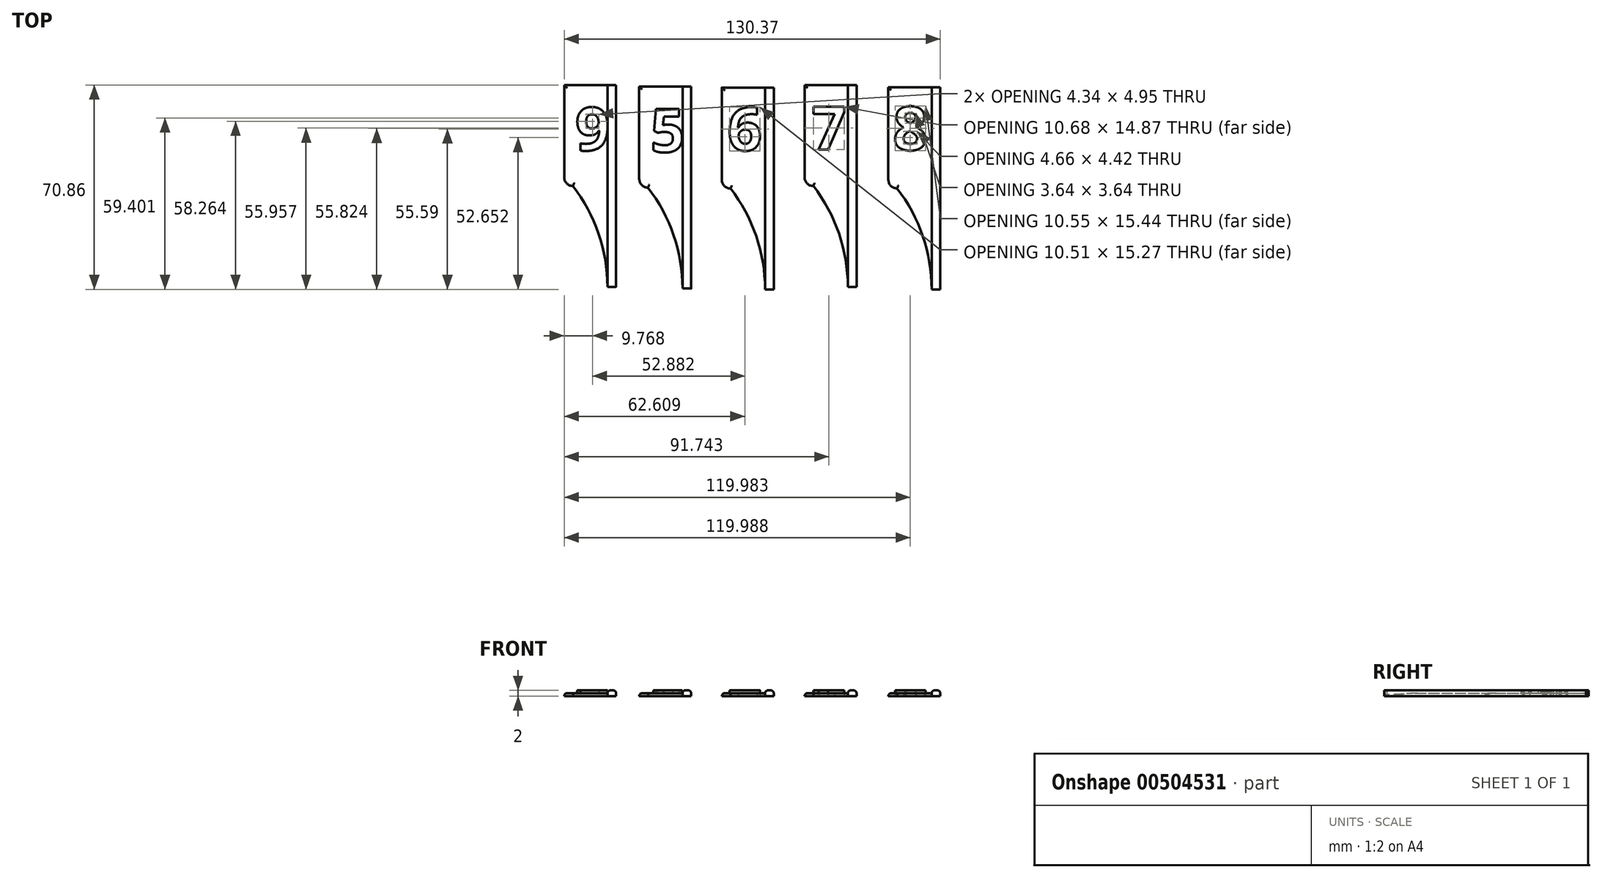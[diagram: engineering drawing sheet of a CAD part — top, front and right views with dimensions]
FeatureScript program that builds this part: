
annotation { "Feature Type Name" : "Feature", "Feature Type Description" : "" }
export const myFeature = defineFeature(function(context is Context, id is Id, definition is map)
    precondition{}
    {
        {
            var Q0;
            Q0=qCreatedBy(makeId("Top.planeOp"),FACE);
            var sketch = newSketch(context, id + "F0", { "sketchPlane" : qUnion([Q0])});
            skLineSegment(sketch, "E0.bottom", {"start": v(-42.45, -18.74) * mm, "end": v(-30.45, -18.74) * mm});
            skLineSegment(sketch, "E0.top", {"start": v(-45.45, 16.26) * mm, "end": v(-30.45, 16.26) * mm});
            skLineSegment(sketch, "E0.left", {"start": v(-45.45, -15.74) * mm, "end": v(-45.45, 16.26) * mm});
            skLineSegment(sketch, "E0.right", {"start": v(-30.45, -18.74) * mm, "end": v(-30.45, 16.26) * mm});
            skLineSegment(sketch, "E1.bottom", {"start": v(-30.45, 16.26) * mm, "end": v(-27.45, 16.26) * mm});
            skLineSegment(sketch, "E1.top", {"start": v(-30.45, -53.74) * mm, "end": v(-27.45, -53.74) * mm});
            skLineSegment(sketch, "E1.left", {"start": v(-30.45, 16.26) * mm, "end": v(-30.45, -53.74) * mm});
            skLineSegment(sketch, "E1.right", {"start": v(-27.45, 16.26) * mm, "end": v(-27.45, -53.74) * mm});
            skPoint(sketch, "E2.visualSharp", {"position": v(-45.45, -18.74) * mm});
            skArc(sketch, "E2.filletArc", {"start": v(-45.45, -15.74) * mm, "mid": v(-44.57, -17.86) * mm, "end": v(-42.45, -18.74) * mm});
            skArc(sketch, "E3", {"start": v(-30.45, -53.74) * mm, "mid": v(-33.53, -35.24) * mm, "end": v(-42.45, -18.74) * mm});
            skText(sketch, "E4", { "text": "5", "fontName": "OpenSans-Bold.ttf"});
            skLineSegment(sketch, "E5.bottom", {"start": v(-13.82, -19.04) * mm, "end": v(-1.82, -19.04) * mm});
            skLineSegment(sketch, "E5.top", {"start": v(-16.82, 15.96) * mm, "end": v(-1.82, 15.96) * mm});
            skLineSegment(sketch, "E5.left", {"start": v(-16.82, -16.04) * mm, "end": v(-16.82, 15.96) * mm});
            skLineSegment(sketch, "E5.right", {"start": v(-1.82, -19.04) * mm, "end": v(-1.82, 15.96) * mm});
            skLineSegment(sketch, "E6.bottom", {"start": v(-1.82, 15.96) * mm, "end": v(1.18, 15.96) * mm});
            skLineSegment(sketch, "E6.top", {"start": v(-1.82, -54.04) * mm, "end": v(1.18, -54.04) * mm});
            skLineSegment(sketch, "E6.left", {"start": v(-1.82, 15.96) * mm, "end": v(-1.82, -54.04) * mm});
            skLineSegment(sketch, "E6.right", {"start": v(1.18, 15.96) * mm, "end": v(1.18, -54.04) * mm});
            skPoint(sketch, "E7.visualSharp", {"position": v(-16.82, -19.04) * mm});
            skArc(sketch, "E7.filletArc", {"start": v(-16.82, -16.04) * mm, "mid": v(-15.94, -18.16) * mm, "end": v(-13.82, -19.04) * mm});
            skArc(sketch, "E8", {"start": v(-1.82, -54.04) * mm, "mid": v(-4.9, -35.54) * mm, "end": v(-13.82, -19.04) * mm});
            skText(sketch, "E9", { "text": "6", "fontName": "OpenSans-Bold.ttf"});
            skLineSegment(sketch, "E10.bottom", {"start": v(14.88, -18.18) * mm, "end": v(26.88, -18.18) * mm});
            skLineSegment(sketch, "E10.top", {"start": v(11.88, 16.82) * mm, "end": v(26.88, 16.82) * mm});
            skLineSegment(sketch, "E10.left", {"start": v(11.88, -15.18) * mm, "end": v(11.88, 16.82) * mm});
            skLineSegment(sketch, "E10.right", {"start": v(26.88, -18.18) * mm, "end": v(26.88, 16.82) * mm});
            skLineSegment(sketch, "E11.bottom", {"start": v(26.88, 16.82) * mm, "end": v(29.88, 16.82) * mm});
            skLineSegment(sketch, "E11.top", {"start": v(26.88, -53.18) * mm, "end": v(29.88, -53.18) * mm});
            skLineSegment(sketch, "E11.left", {"start": v(26.88, 16.82) * mm, "end": v(26.88, -53.18) * mm});
            skLineSegment(sketch, "E11.right", {"start": v(29.88, 16.82) * mm, "end": v(29.88, -53.18) * mm});
            skPoint(sketch, "E12.visualSharp", {"position": v(11.88, -18.18) * mm});
            skArc(sketch, "E12.filletArc", {"start": v(11.88, -15.18) * mm, "mid": v(12.76, -17.3) * mm, "end": v(14.88, -18.18) * mm});
            skArc(sketch, "E13", {"start": v(26.88, -53.18) * mm, "mid": v(23.8, -34.68) * mm, "end": v(14.88, -18.18) * mm});
            skLineSegment(sketch, "E14.bottom", {"start": v(43.91, -19.02) * mm, "end": v(55.91, -19.02) * mm});
            skLineSegment(sketch, "E14.top", {"start": v(40.91, 15.98) * mm, "end": v(55.91, 15.98) * mm});
            skLineSegment(sketch, "E14.left", {"start": v(40.91, -16.02) * mm, "end": v(40.91, 15.98) * mm});
            skLineSegment(sketch, "E14.right", {"start": v(55.91, -19.02) * mm, "end": v(55.91, 15.98) * mm});
            skLineSegment(sketch, "E15.bottom", {"start": v(55.91, 15.98) * mm, "end": v(58.91, 15.98) * mm});
            skLineSegment(sketch, "E15.top", {"start": v(55.91, -54.02) * mm, "end": v(58.91, -54.02) * mm});
            skLineSegment(sketch, "E15.left", {"start": v(55.91, 15.98) * mm, "end": v(55.91, -54.02) * mm});
            skLineSegment(sketch, "E15.right", {"start": v(58.91, 15.98) * mm, "end": v(58.91, -54.02) * mm});
            skPoint(sketch, "E16.visualSharp", {"position": v(40.91, -19.02) * mm});
            skArc(sketch, "E16.filletArc", {"start": v(40.91, -16.02) * mm, "mid": v(41.8, -18.14) * mm, "end": v(43.91, -19.02) * mm});
            skArc(sketch, "E17", {"start": v(55.91, -54.02) * mm, "mid": v(52.83, -35.52) * mm, "end": v(43.91, -19.02) * mm});
            skText(sketch, "E18", { "text": "7", "fontName": "OpenSans-Bold.ttf"});
            skText(sketch, "E19", { "text": "8", "fontName": "OpenSans-Bold.ttf"});
            skLineSegment(sketch, "E20.bottom", {"start": v(-68.46, -18.18) * mm, "end": v(-56.46, -18.18) * mm});
            skLineSegment(sketch, "E20.top", {"start": v(-71.46, 16.82) * mm, "end": v(-56.46, 16.82) * mm});
            skLineSegment(sketch, "E20.left", {"start": v(-71.46, -15.18) * mm, "end": v(-71.46, 16.82) * mm});
            skLineSegment(sketch, "E20.right", {"start": v(-56.46, -18.18) * mm, "end": v(-56.46, 16.82) * mm});
            skLineSegment(sketch, "E21.bottom", {"start": v(-56.46, 16.82) * mm, "end": v(-53.46, 16.82) * mm});
            skLineSegment(sketch, "E21.top", {"start": v(-56.46, -53.18) * mm, "end": v(-53.46, -53.18) * mm});
            skLineSegment(sketch, "E21.left", {"start": v(-56.46, 16.82) * mm, "end": v(-56.46, -53.18) * mm});
            skLineSegment(sketch, "E21.right", {"start": v(-53.46, 16.82) * mm, "end": v(-53.46, -53.18) * mm});
            skPoint(sketch, "E22.visualSharp", {"position": v(-71.46, -18.18) * mm});
            skArc(sketch, "E22.filletArc", {"start": v(-71.46, -15.18) * mm, "mid": v(-70.58, -17.3) * mm, "end": v(-68.46, -18.18) * mm});
            skArc(sketch, "E23", {"start": v(-56.46, -53.18) * mm, "mid": v(-59.55, -34.68) * mm, "end": v(-68.46, -18.18) * mm});
            skText(sketch, "E24", { "text": "9", "fontName": "OpenSans-Bold.ttf"});
            skPoint(sketch, "E25.visualSharp", {"position": v(-42.83, -18.49) * mm});
            const initialGuessF0  = {"E4": [-0.04157, -0.0064, 1, 0, 0.01502], "E9": [-0.01484, -0.00588, 1, 0, 0.01502], "E18": [0.01438, -0.00552, 1, 0, 0.01502], "E19": [0.04251, -0.00573, 1, 0, 0.01517], "E24": [-0.06758, -0.00584, 1, 0, 0.01502]};
            skSetInitialGuess(sketch, initialGuessF0);
            skSolve(sketch);
        }
        {
            var Q0;
            {var subQ0=sQuery(id+"F0.wireOp",EDGE,"E0.bottom");Q0=makeQuery(id+"F0.imprint","IMPRINT",FACE,{"disambiguationData":[TD([[makeQuery(id+"F0.imprint","IMPRINT",EDGE,{"derivedFrom":subQ0}),1.0]])]});}
            extrude(context, id + "F1", {"entities" : qUnion([Q0]), "depth" : 1 * mm});
        }
        {
            var Q0;
            {var subQ3=sQuery(id+"F0.wireOp",EDGE,"E1.bottom");Q0=makeQuery(id+"F0.imprint","IMPRINT",FACE,{"disambiguationData":[TD([[makeQuery(id+"F0.imprint","IMPRINT",EDGE,{"derivedFrom":subQ3}),-1.0]])]});}
            extrude(context, id + "F2", {"entities" : qUnion([Q0]), "operationType" : NewBodyOperationType.ADD, "depth" : 2 * mm});
        }
        {
            var Q0;
            Q0=makeQuery(id+"F0.imprint","IMPRINT",FACE,{"disambiguationData":[TD([[makeQuery(id+"F0.imprint","IMPRINT",EDGE,{"derivedFrom":sQuery(id+"F0.wireOp",EDGE,"E4.sketch_text.stroke-0")}),-1.0]])]});
            extrude(context, id + "F3", {"entities" : qUnion([Q0]), "operationType" : NewBodyOperationType.ADD, "depth" : 2 * mm});
        }
        {
            var Q0;
            {var subQ0=sQuery(id+"F0.wireOp",EDGE,"E0.bottom");Q0=makeQuery(id+"F0.imprint","IMPRINT",FACE,{"disambiguationData":[TD([[makeQuery(id+"F0.imprint","IMPRINT",EDGE,{"derivedFrom":subQ0}),-1.0]])]});}
            extrude(context, id + "F4", {"entities" : qUnion([Q0]), "operationType" : NewBodyOperationType.ADD, "depth" : 1 * mm});
        }
        {
            var Q0;
            Q0=makeQuery(id+"F2.opExtrude","CAP_EDGE",EDGE,{"disambiguationData":[OSD([sQuery(id+"F0.wireOp",EDGE,"E1.right")])],"isStart":false});
            fillet(context, id + "F5", {"entities" : qUnion([Q0]), "radius" : 1 * mm, "tangentPropagation" : true, "allowEdgeOverflow" : false});
        }
        {
            var Q0;
            Q0=makeQuery(id+"F2.opExtrude","CAP_EDGE",EDGE,{"disambiguationData":[OSD([sQuery(id+"F0.wireOp",EDGE,"E1.left")])],"isStart":false});
            fillet(context, id + "F6", {"entities" : qUnion([Q0]), "radius" : 1 * mm, "tangentPropagation" : true, "allowEdgeOverflow" : false});
        }
        {
            var Q0;
            Q0=makeQuery(id+"F1.opExtrude","CAP_EDGE",EDGE,{"disambiguationData":[OSD([sQuery(id+"F0.wireOp",EDGE,"E2.filletArc")])],"isStart":false});
            var Q1;
            Q1=makeQuery(id+"F4.opExtrude","CAP_EDGE",EDGE,{"disambiguationData":[OSD([sQuery(id+"F0.wireOp",EDGE,"E3")])],"isStart":false});
            var Q2;
            Q2=makeQuery(id+"F1.opExtrude","CAP_EDGE",EDGE,{"disambiguationData":[OSD([sQuery(id+"F0.wireOp",EDGE,"E0.top")])],"isStart":false});
            var Q3;
            Q3=makeQuery(id+"F1.opExtrude","CAP_EDGE",EDGE,{"disambiguationData":[OSD([sQuery(id+"F0.wireOp",EDGE,"E0.left")])],"isStart":false});
            fillet(context, id + "F7", {"entities" : qUnion([Q0, Q1, Q2, Q3]), "radius" : 1 * mm, "tangentPropagation" : true, "allowEdgeOverflow" : false});
        }
        {
            var Q0;
            {var subQ2=sQuery(id+"F0.wireOp",EDGE,"E5.bottom");Q0=makeQuery(id+"F0.imprint","IMPRINT",FACE,{"disambiguationData":[TD([[makeQuery(id+"F0.imprint","IMPRINT",EDGE,{"derivedFrom":subQ2}),1.0]])]});}
            var Q1;
            {var subQ1=sQuery(id+"F0.wireOp",EDGE,"E10.bottom");Q1=makeQuery(id+"F0.imprint","IMPRINT",FACE,{"disambiguationData":[TD([[makeQuery(id+"F0.imprint","IMPRINT",EDGE,{"derivedFrom":subQ1}),1.0]])]});}
            var Q2;
            {var subQ0=sQuery(id+"F0.wireOp",EDGE,"E14.bottom");Q2=makeQuery(id+"F0.imprint","IMPRINT",FACE,{"disambiguationData":[TD([[makeQuery(id+"F0.imprint","IMPRINT",EDGE,{"derivedFrom":subQ0}),1.0]])]});}
            var Q3;
            {var subQ0=sQuery(id+"F0.wireOp",EDGE,"E14.bottom");Q3=makeQuery(id+"F0.imprint","IMPRINT",FACE,{"disambiguationData":[TD([[makeQuery(id+"F0.imprint","IMPRINT",EDGE,{"derivedFrom":subQ0}),-1.0]])]});}
            var Q4;
            {var subQ0=sQuery(id+"F0.wireOp",EDGE,"E10.bottom");Q4=makeQuery(id+"F0.imprint","IMPRINT",FACE,{"disambiguationData":[TD([[makeQuery(id+"F0.imprint","IMPRINT",EDGE,{"derivedFrom":subQ0}),-1.0]])]});}
            var Q5;
            {var subQ0=sQuery(id+"F0.wireOp",EDGE,"E5.bottom");Q5=makeQuery(id+"F0.imprint","IMPRINT",FACE,{"disambiguationData":[TD([[makeQuery(id+"F0.imprint","IMPRINT",EDGE,{"derivedFrom":subQ0}),-1.0]])]});}
            extrude(context, id + "F8", {"entities" : qUnion([Q0, Q1, Q2, Q3, Q4, Q5]), "depth" : 1 * mm});
        }
        {
            var Q0;
            Q0=makeQuery(id+"F0.imprint","IMPRINT",FACE,{"disambiguationData":[TD([[makeQuery(id+"F0.imprint","IMPRINT",EDGE,{"derivedFrom":sQuery(id+"F0.wireOp",EDGE,"E9.sketch_text.stroke-0")}),-1.0]])]});
            var Q1;
            Q1=makeQuery(id+"F0.imprint","IMPRINT",FACE,{"disambiguationData":[TD([[makeQuery(id+"F0.imprint","IMPRINT",EDGE,{"derivedFrom":sQuery(id+"F0.wireOp",EDGE,"E18.sketch_text.stroke-0")}),-1.0]])]});
            var Q2;
            Q2=makeQuery(id+"F0.imprint","IMPRINT",FACE,{"disambiguationData":[TD([[makeQuery(id+"F0.imprint","IMPRINT",EDGE,{"derivedFrom":sQuery(id+"F0.wireOp",EDGE,"E19.sketch_text.stroke-0")}),-1.0]])]});
            extrude(context, id + "F9", {"entities" : qUnion([Q0, Q1, Q2]), "depth" : 2 * mm});
        }
        {
            var Q0;
            {var subQ3=sQuery(id+"F0.wireOp",EDGE,"E6.bottom");Q0=makeQuery(id+"F0.imprint","IMPRINT",FACE,{"disambiguationData":[TD([[makeQuery(id+"F0.imprint","IMPRINT",EDGE,{"derivedFrom":subQ3}),-1.0]])]});}
            var Q1;
            {var subQ3=sQuery(id+"F0.wireOp",EDGE,"E11.bottom");Q1=makeQuery(id+"F0.imprint","IMPRINT",FACE,{"disambiguationData":[TD([[makeQuery(id+"F0.imprint","IMPRINT",EDGE,{"derivedFrom":subQ3}),-1.0]])]});}
            var Q2;
            {var subQ3=sQuery(id+"F0.wireOp",EDGE,"E15.bottom");Q2=makeQuery(id+"F0.imprint","IMPRINT",FACE,{"disambiguationData":[TD([[makeQuery(id+"F0.imprint","IMPRINT",EDGE,{"derivedFrom":subQ3}),-1.0]])]});}
            extrude(context, id + "F10", {"entities" : qUnion([Q0, Q1, Q2]), "depth" : 2 * mm});
        }
        {
            var Q0;
            Q0=makeQuery(id+"F8.opExtrude","CAP_EDGE",EDGE,{"disambiguationData":[OSD([sQuery(id+"F0.wireOp",EDGE,"E8")])],"isStart":false});
            var Q1;
            Q1=makeQuery(id+"F8.opExtrude","CAP_EDGE",EDGE,{"disambiguationData":[OSD([sQuery(id+"F0.wireOp",EDGE,"E7.filletArc")])],"isStart":false});
            var Q2;
            Q2=makeQuery(id+"F8.opExtrude","CAP_EDGE",EDGE,{"disambiguationData":[OSD([sQuery(id+"F0.wireOp",EDGE,"E5.top")])],"isStart":false});
            var Q3;
            Q3=makeQuery(id+"F8.opExtrude","CAP_EDGE",EDGE,{"disambiguationData":[OSD([sQuery(id+"F0.wireOp",EDGE,"E14.top")])],"isStart":false});
            var Q4;
            Q4=makeQuery(id+"F8.opExtrude","CAP_EDGE",EDGE,{"disambiguationData":[OSD([sQuery(id+"F0.wireOp",EDGE,"E5.left")])],"isStart":false});
            var Q5;
            Q5=makeQuery(id+"F8.opExtrude","CAP_EDGE",EDGE,{"disambiguationData":[OSD([sQuery(id+"F0.wireOp",EDGE,"E10.top")])],"isStart":false});
            var Q6;
            Q6=makeQuery(id+"F8.opExtrude","CAP_EDGE",EDGE,{"disambiguationData":[OSD([sQuery(id+"F0.wireOp",EDGE,"E10.left")])],"isStart":false});
            var Q7;
            Q7=makeQuery(id+"F8.opExtrude","CAP_EDGE",EDGE,{"disambiguationData":[OSD([sQuery(id+"F0.wireOp",EDGE,"E12.filletArc")])],"isStart":false});
            var Q8;
            Q8=makeQuery(id+"F8.opExtrude","CAP_EDGE",EDGE,{"disambiguationData":[OSD([sQuery(id+"F0.wireOp",EDGE,"E13")])],"isStart":false});
            var Q9;
            Q9=makeQuery(id+"F8.opExtrude","CAP_EDGE",EDGE,{"disambiguationData":[OSD([sQuery(id+"F0.wireOp",EDGE,"E14.left")])],"isStart":false});
            var Q10;
            Q10=makeQuery(id+"F8.opExtrude","CAP_EDGE",EDGE,{"disambiguationData":[OSD([sQuery(id+"F0.wireOp",EDGE,"E16.filletArc")])],"isStart":false});
            var Q11;
            Q11=makeQuery(id+"F8.opExtrude","CAP_EDGE",EDGE,{"disambiguationData":[OSD([sQuery(id+"F0.wireOp",EDGE,"E17")])],"isStart":false});
            fillet(context, id + "F11", {"entities" : qUnion([Q0, Q1, Q2, Q3, Q4, Q5, Q6, Q7, Q8, Q9, Q10, Q11]), "radius" : 1 * mm, "tangentPropagation" : true, "allowEdgeOverflow" : false});
        }
        {
            var Q0;
            Q0=makeQuery(id+"F10.opExtrude","CAP_EDGE",EDGE,{"disambiguationData":[OSD([sQuery(id+"F0.wireOp",EDGE,"E15.right")])],"isStart":false});
            var Q1;
            Q1=makeQuery(id+"F10.opExtrude","CAP_EDGE",EDGE,{"disambiguationData":[OSD([sQuery(id+"F0.wireOp",EDGE,"E15.left")])],"isStart":false});
            var Q2;
            Q2=makeQuery(id+"F10.opExtrude","CAP_EDGE",EDGE,{"disambiguationData":[OSD([sQuery(id+"F0.wireOp",EDGE,"E11.right")])],"isStart":false});
            var Q3;
            Q3=makeQuery(id+"F10.opExtrude","CAP_EDGE",EDGE,{"disambiguationData":[OSD([sQuery(id+"F0.wireOp",EDGE,"E6.right")])],"isStart":false});
            var Q4;
            Q4=makeQuery(id+"F10.opExtrude","CAP_EDGE",EDGE,{"disambiguationData":[OSD([sQuery(id+"F0.wireOp",EDGE,"E6.left")])],"isStart":false});
            fillet(context, id + "F12", {"entities" : qUnion([Q0, Q1, Q2, Q3, Q4]), "radius" : 1 * mm, "tangentPropagation" : true, "allowEdgeOverflow" : false});
        }
        {
            var Q0;
            Q0=makeQuery(id+"F10.opExtrude","CAP_EDGE",EDGE,{"disambiguationData":[OSD([sQuery(id+"F0.wireOp",EDGE,"E11.left")])],"isStart":false});
            fillet(context, id + "F13", {"entities" : qUnion([Q0]), "radius" : 1 * mm, "tangentPropagation" : true, "allowEdgeOverflow" : false});
        }
        {
            var Q0;
            {var subQ7=sQuery(id+"F0.wireOp",EDGE,"E20.bottom");Q0=makeQuery(id+"F0.imprint","IMPRINT",FACE,{"disambiguationData":[TD([[makeQuery(id+"F0.imprint","IMPRINT",EDGE,{"derivedFrom":subQ7}),1.0]])]});}
            extrude(context, id + "F14", {"entities" : qUnion([Q0]), "depth" : 1 * mm});
        }
        {
            var Q0;
            {var subQ4=sQuery(id+"F0.wireOp",EDGE,"E24.sketch_text.stroke-1");Q0=makeQuery(id+"F0.imprint","IMPRINT",FACE,{"disambiguationData":[TD([[makeQuery(id+"F0.imprint","IMPRINT",EDGE,{"derivedFrom":subQ4}),-1.0]])]});}
            extrude(context, id + "F15", {"entities" : qUnion([Q0]), "operationType" : NewBodyOperationType.ADD, "depth" : 2 * mm});
        }
        {
            var Q0;
            {var subQ0=sQuery(id+"F0.wireOp",EDGE,"E20.bottom");Q0=makeQuery(id+"F0.imprint","IMPRINT",FACE,{"disambiguationData":[TD([[makeQuery(id+"F0.imprint","IMPRINT",EDGE,{"derivedFrom":subQ0}),-1.0]])]});}
            extrude(context, id + "F16", {"entities" : qUnion([Q0]), "operationType" : NewBodyOperationType.ADD, "depth" : 1 * mm});
        }
        {
            var Q0;
            {var subQ4=sQuery(id+"F0.wireOp",EDGE,"E21.bottom");Q0=makeQuery(id+"F0.imprint","IMPRINT",FACE,{"disambiguationData":[TD([[makeQuery(id+"F0.imprint","IMPRINT",EDGE,{"derivedFrom":subQ4}),-1.0]])]});}
            extrude(context, id + "F17", {"entities" : qUnion([Q0]), "depth" : 2 * mm});
        }
        {
            var Q0;
            Q0=makeQuery(id+"F14.opExtrude","CAP_EDGE",EDGE,{"disambiguationData":[OSD([sQuery(id+"F0.wireOp",EDGE,"E20.left")])],"isStart":false});
            var Q1;
            Q1=makeQuery(id+"F16.opExtrude","CAP_EDGE",EDGE,{"disambiguationData":[OSD([sQuery(id+"F0.wireOp",EDGE,"E23")])],"isStart":false});
            var Q2;
            Q2=makeQuery(id+"F14.opExtrude","CAP_EDGE",EDGE,{"disambiguationData":[OSD([sQuery(id+"F0.wireOp",EDGE,"E20.top")])],"isStart":false});
            var Q3;
            {var subQ0=sQuery(id+"F0.wireOp",EDGE,"E21.left");var subQ1=makeQuery(id+"F0.imprint","INTERSECT",VERTEX,{"derivedFrom":[sQuery(id+"F0.wireOp",EDGE,"E20.bottom"),subQ0]});Q3=makeQuery(id+"F17.opExtrude","CAP_EDGE",EDGE,{"disambiguationData":[OSD([subQ0]),TDD([makeQuery(id+"F0.imprint","IMPRINT",EDGE,{"disambiguationData":[TD([[subQ1,1.0]])],"derivedFrom":subQ0}),makeQuery(id+"F0.imprint","IMPRINT",EDGE,{"disambiguationData":[TD([[subQ1,-1.0]])],"derivedFrom":subQ0})])],"isStart":false});}
            var Q4;
            Q4=makeQuery(id+"F17.opExtrude","CAP_EDGE",EDGE,{"disambiguationData":[OSD([sQuery(id+"F0.wireOp",EDGE,"E21.right")])],"isStart":false});
            fillet(context, id + "F18", {"entities" : qUnion([Q0, Q1, Q2, Q3, Q4]), "radius" : 1 * mm, "tangentPropagation" : true, "allowEdgeOverflow" : false});
        }
    });
